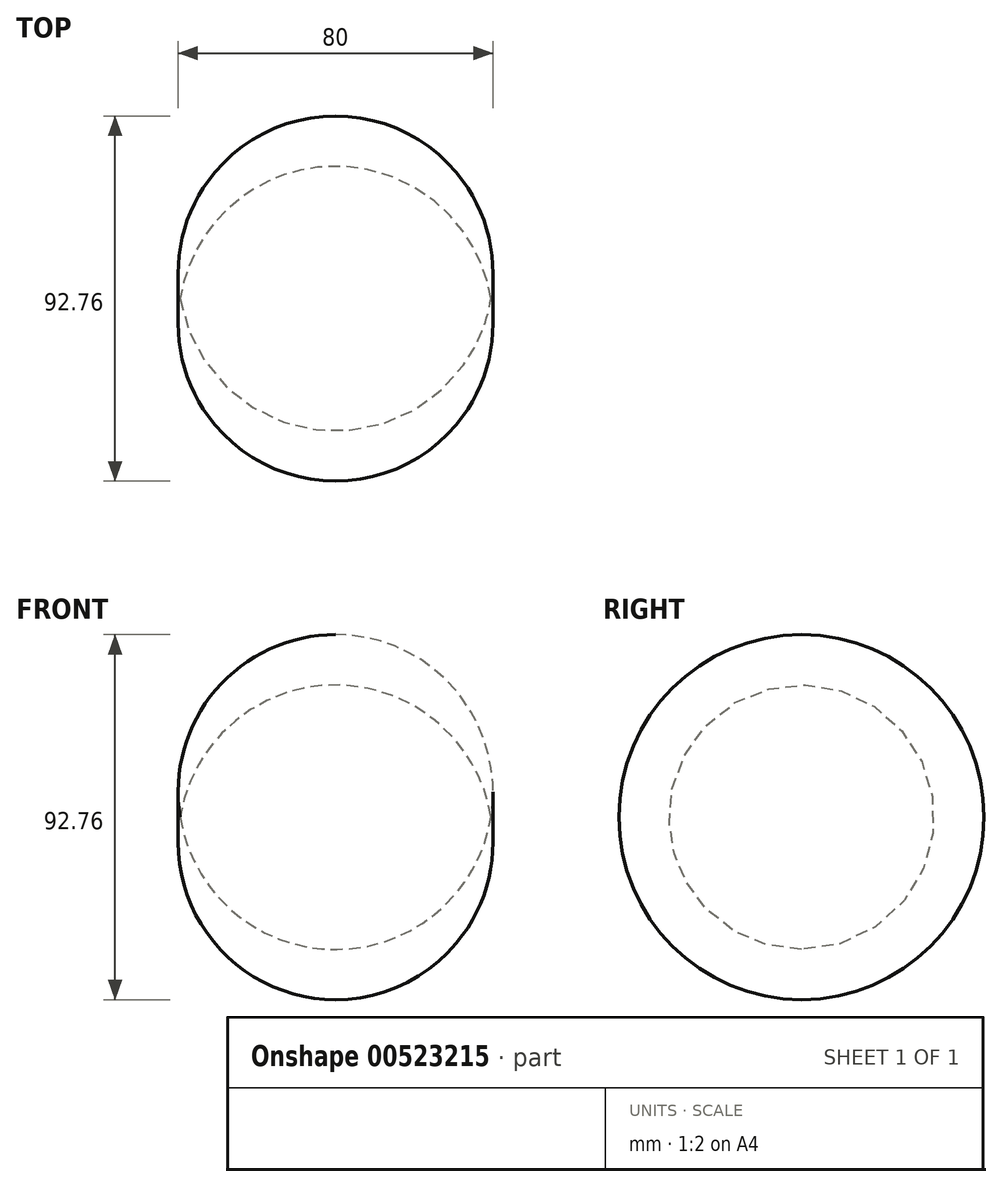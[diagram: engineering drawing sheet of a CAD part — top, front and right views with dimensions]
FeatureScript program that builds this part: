
annotation { "Feature Type Name" : "Feature", "Feature Type Description" : "" }
export const myFeature = defineFeature(function(context is Context, id is Id, definition is map)
    precondition{}
    {
        {
            var Q0;
            Q0=qCreatedBy(makeId("Front.planeOp"),FACE);
            var sketch = newSketch(context, id + "F0", { "sketchPlane" : qUnion([Q0])});
            skLineSegment(sketch, "E0", {"start": v(-46.44, 0) * mm, "end": v(50.42, 0) * mm, "construction": true});
            skArc(sketch, "E1", {"start": v(39.02, 0) * mm, "mid": v(-0.46, 33.62) * mm, "end": v(-39.95, 0) * mm});
            skLineSegment(sketch, "E2", {"start": v(-39.95, 0) * mm, "end": v(39.02, 0) * mm});
            skSolve(sketch);
        }
        {
            var Q0;
            Q0=qSketchRegion(id+"F0",true);
            var Q1;
            Q1=sQuery(id+"F0.wireOp",EDGE,"E0");
            revolve(context, id + "F1", {"entities" : qUnion([Q0]), "axis" : qUnion([Q1]), "revolveType" : RevolveType.FULL});
        }
    });
